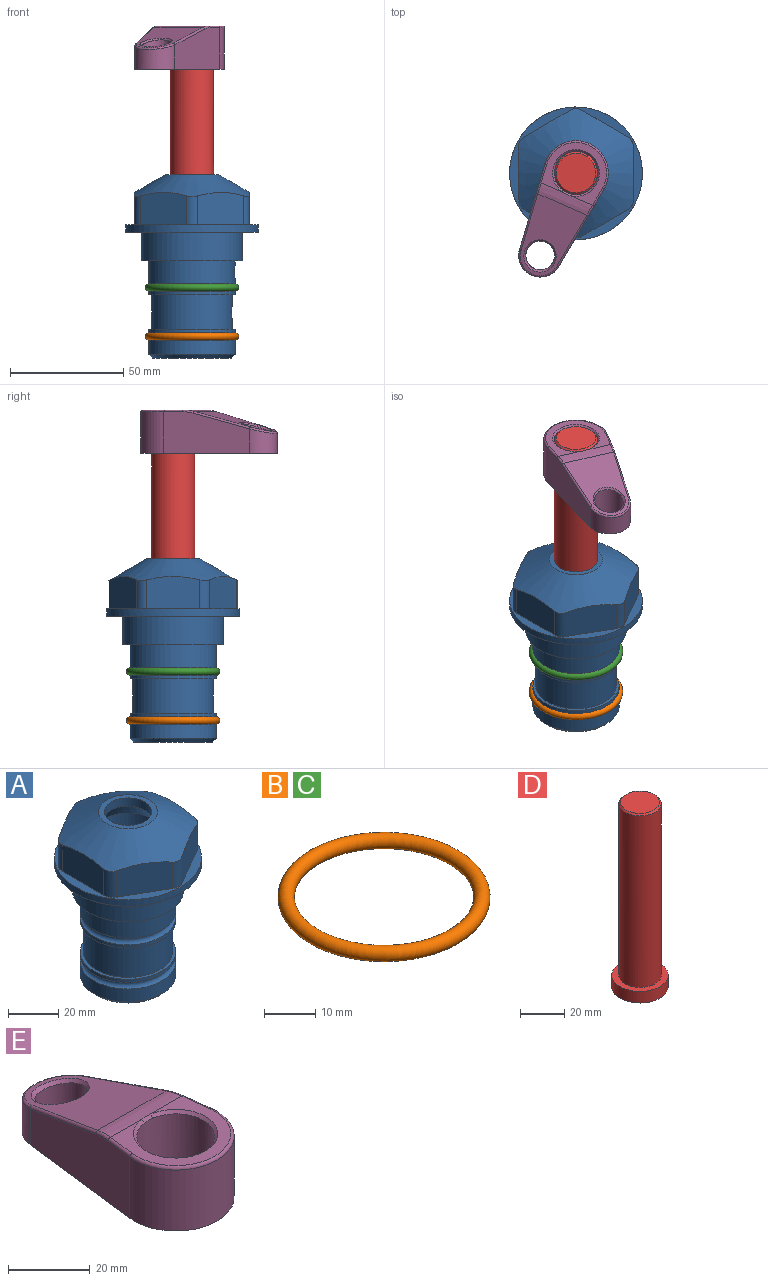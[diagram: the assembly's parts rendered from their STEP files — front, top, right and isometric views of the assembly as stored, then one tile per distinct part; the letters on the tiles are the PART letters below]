
ASSEMBLY  parts=5 mates=4
PART A: 36 faces, bbox 58.7x58.7x81 mm
  f0: cylinder r=17.78mm len=35.56mm, axis (0,0,1), area 1670.8mm2, adj f23,f24,f31
  f1: cylinder r=19.05mm len=38.1mm, axis (0,0,1), area 1191.9mm2, adj f26,f27,f30
  f2: plane 58.66x58.66mm, normal (0,0,-1), area 1150.6mm2, adj f3,f28
  f3: cylinder r=29.33mm len=58.66mm, axis (0,0,-1), area 585.1mm2, adj f2,f4
  f4: plane 58.66x58.66mm, normal (0,0,1), area 475.9mm2, adj f3,f5,f6,f7,f8,f9,f10,f11
  f5: plane 20.32x14.34mm, normal (-0.5,0.87,0), area 324.4mm2, adj f4,f15,f16,f17
  f6: plane 20.32x14.34mm, normal (0.5,0.87,0), area 324.4mm2, adj f4,f14,f15,f17
  f7: plane 23.48x14.34mm, normal (1,0,0), area 324.4mm2, adj f4,f13,f14,f17
  f8: plane 20.32x14.34mm, normal (0.5,-0.87,0), area 324.4mm2, adj f4,f12,f13,f17
  f9: plane 20.32x14.34mm, normal (-0.5,-0.87,0), area 324.4mm2, adj f4,f11,f12,f17
  f10: plane 23.48x14.34mm, normal (-1,0,0), area 324.4mm2, adj f4,f11,f16,f17
  f11: cylinder r=5.08mm len=12.85mm, axis (0,0,-1), area 67.2mm2, adj f4,f9,f10,f17
  f12: cylinder r=5.08mm len=12.85mm, axis (0,0,-1), area 67.2mm2, adj f4,f8,f9,f17
  f13: cylinder r=5.08mm len=12.85mm, axis (0,0,-1), area 67.2mm2, adj f4,f7,f8,f17
  f14: cylinder r=5.08mm len=12.85mm, axis (0,0,-1), area 67.2mm2, adj f4,f6,f7,f17
  f15: cylinder r=5.08mm len=12.85mm, axis (0,0,-1), area 67.2mm2, adj f4,f5,f6,f17
  f16: cylinder r=5.08mm len=12.85mm, axis (0,0,-1), area 67.2mm2, adj f4,f5,f10,f17
  f17: cone r=11.73mm half-angle=60deg, axis (0,0,-1), area 2071.8mm2, adj f5,f6,f7,f8,f9,f10,f11,f12
  f18: plane 23.46x23.46mm, normal (0,0,1), area 147.4mm2, adj f17,f35
  f19: plane 34.93x34.93mm, normal (0,0,-1), area 958mm2, adj f29
  f20: cylinder r=19.05mm len=38.1mm, axis (0,0,1), area 760.1mm2, adj f21,f29
  f21: torus R=19.05mm, axis (0,0,1), area 565.3mm2, adj f20,f22
  f22: cylinder r=19.05mm len=38.1mm, axis (0,0,1), area 190mm2, adj f21,f23
  f23: plane 38.1x38.1mm, normal (0,0,1), area 146.9mm2, adj f0,f22
  f24: plane 38.1x38.1mm, normal (0,0,-1), area 146.9mm2, adj f0,f25
  f25: cylinder r=19.05mm len=38.1mm, axis (0,0,1), area 190mm2, adj f24,f26
  f26: torus R=19.05mm, axis (0,0,1), area 565.3mm2, adj f1,f25
  f27: plane 44.45x44.45mm, normal (0,0,-1), area 411.7mm2, adj f1,f28
  f28: cylinder r=22.23mm len=44.45mm, axis (0,0,1), area 1773.5mm2, adj f2,f27
  f29: cone r=19.05mm half-angle=45deg, axis (0,0,1), area 257.5mm2, adj f19,f20
  f30: cylinder r=3.17mm len=6.75mm, axis (-1,0,0), area 128mm2, adj f1,f33
  f31: cylinder r=3.17mm len=6.35mm, axis (-1,0,0), area 102.5mm2, adj f0,f33
  f32: plane 25.4x25.4mm, normal (0,0,1), area 506.7mm2, adj f33
  f33: cylinder r=12.7mm len=66.42mm, axis (0,0,-1), area 5236.2mm2, adj f30,f31,f32,f34
  f34: cone r=9.53mm half-angle=30deg, axis (0,0,-1), area 443.4mm2, adj f33,f35
  f35: cylinder r=9.53mm len=19.05mm, axis (0,0,-1), area 240.9mm2, adj f18,f34
PART B: 1 faces, bbox 44.7x44.7x3.2 mm
  f0: torus R=19.05mm, axis (0,0,1), area 1193.9mm2
PART C: same geometry as B
PART D: 6 faces, bbox 25.4x25.4x101.6 mm
  f0: plane 17.46x17.46mm, normal (0,0,1), area 239.5mm2, adj f5
  f1: plane 25.4x25.4mm, normal (0,0,-1), area 506.7mm2, adj f2
  f2: cylinder r=12.7mm len=25.4mm, axis (0,0,1), area 506.7mm2, adj f1,f3
  f3: plane 25.4x25.4mm, normal (0,0,1), area 221.7mm2, adj f2,f4
  f4: cylinder r=9.53mm len=94.46mm, axis (0,0,1), area 5653mm2, adj f3,f5
  f5: cone r=8.73mm half-angle=45deg, axis (0,0,-1), area 64.4mm2, adj f0,f4
PART E: 31 faces, bbox 31.7x65.5x19.8 mm
  f0: plane 39.12x18.26mm, normal (0.99,0.12,0), area 612.2mm2, adj f1,f4,f7,f11,f13,f15
  f1: cylinder r=9.53mm len=18.91mm, axis (0,0,-1), area 296.1mm2, adj f0,f2,f7,f17
  f2: plane 39.12x18.26mm, normal (-0.99,0.12,0), area 612.2mm2, adj f1,f4,f7,f12,f14,f16
  f3: cylinder r=6.35mm len=12.7mm, axis (0,0,-1), area 362.4mm2, adj f7,f18
  f4: cylinder r=14.29mm len=28.58mm, axis (0,0,-1), area 882.2mm2, adj f0,f2,f7,f10
  f5: cylinder r=9.53mm len=19.05mm, axis (0,0,-1), area 1092.6mm2, adj f7,f19,f20
  f6: plane 26.99x23.69mm, normal (0,0,1), area 216.2mm2, adj f9,f10,f11,f12,f19
  f7: plane 63.5x28.58mm, normal (0,0,-1), area 661.8mm2, adj f0,f1,f2,f3,f4,f5,f22,f23
  f8: plane 33.52x23.6mm, normal (0,0.26,0.97), area 486mm2, adj f9,f15,f16,f17,f18
  f9: cylinder r=19.05mm len=24.72mm, axis (1,0,0), area 120.4mm2, adj f6,f8,f13,f14,f20
  f10: torus R=13.49mm, axis (0,0,1), area 59mm2, adj f4,f6,f11,f12
  f11: cylinder r=0.79mm len=8.67mm, axis (0.12,-0.99,0), area 10.8mm2, adj f0,f6,f10,f13
  f12: cylinder r=0.79mm len=8.67mm, axis (0.12,0.99,0), area 10.8mm2, adj f2,f6,f10,f14
  f13: bspline ~4.95x1.42mm, area 6.1mm2, adj f0,f9,f11,f15
  f14: bspline ~4.95x1.42mm, area 6.1mm2, adj f2,f9,f12,f16
  f15: cylinder r=0.79mm len=25.95mm, axis (0.12,-0.96,0.26), area 32.9mm2, adj f0,f8,f13,f17
  f16: cylinder r=0.79mm len=25.95mm, axis (0.12,0.96,-0.26), area 32.9mm2, adj f2,f8,f14,f17
  f17: bspline ~18.91x8.38mm, area 30mm2, adj f1,f8,f15,f16
  f18: bspline ~14.29x14.29mm, area 48.3mm2, adj f3,f8
  f19: cone r=9.53mm half-angle=45deg, axis (0,0,1), area 66.5mm2, adj f5,f6,f20
  f20: bspline ~3.22x0.96mm, area 3.5mm2, adj f5,f9,f19
  f21: plane 2.75x2.72mm, normal (0,0,-1), area 2.9mm2, adj f23,f25,f28
  f22: plane 23.05x15.88mm, normal (-0.99,-0.12,0), area 323.6mm2, adj f7,f25,f26,f27,f28,f29
  f23: plane 23.05x15.88mm, normal (0.99,-0.12,0), area 323.6mm2, adj f7,f21,f25,f27,f28,f30
  f24: cylinder r=9.53mm len=10.69mm, axis (0,0,-1), area 114.7mm2, adj f7,f27,f29,f30
  f25: cylinder r=12.7mm len=20.59mm, axis (0,0,-1), area 381.1mm2, adj f7,f21,f22,f23,f26,f28
  f26: plane 2.75x2.72mm, normal (0,0,-1), area 2.9mm2, adj f22,f25,f28
  f27: plane 19.72x18.37mm, normal (0,-0.26,-0.97), area 291.8mm2, adj f22,f23,f24,f28,f29,f30
  f28: cylinder r=15.88mm len=19.92mm, axis (1,0,0), area 54.8mm2, adj f21,f22,f23,f25,f26,f27
  f29: cylinder r=1.59mm len=11mm, axis (0,0,-1), area 34.7mm2, adj f7,f22,f24,f27
  f30: cylinder r=1.59mm len=11mm, axis (0,0,-1), area 34.7mm2, adj f7,f23,f24,f27
PLACE A at identity fixed
PLACE B t=(0,0,-21.59)mm
PLACE C at identity
PLACE D rot(axis=(0,0,1),156.5deg) t=(0,0,27.55)mm
PLACE E rot(axis=(0,0,1),156.5deg) t=(0,0,27.55)mm
MATE fastened C.f0 <-> A.f0  axis (0,0,1) through (0,0,-24.51)mm
MATE fastened D.f2 <-> E.f4  axis (0,0,1) through (0,0,91.05)mm
MATE fastened B.f0 <-> A.f0  axis (0,0,1) through (0,0,-46.1)mm
MATE cylindrical A.f0 <-> D.f2  axis (0,0,1) through (0,0,-50.55)mm
